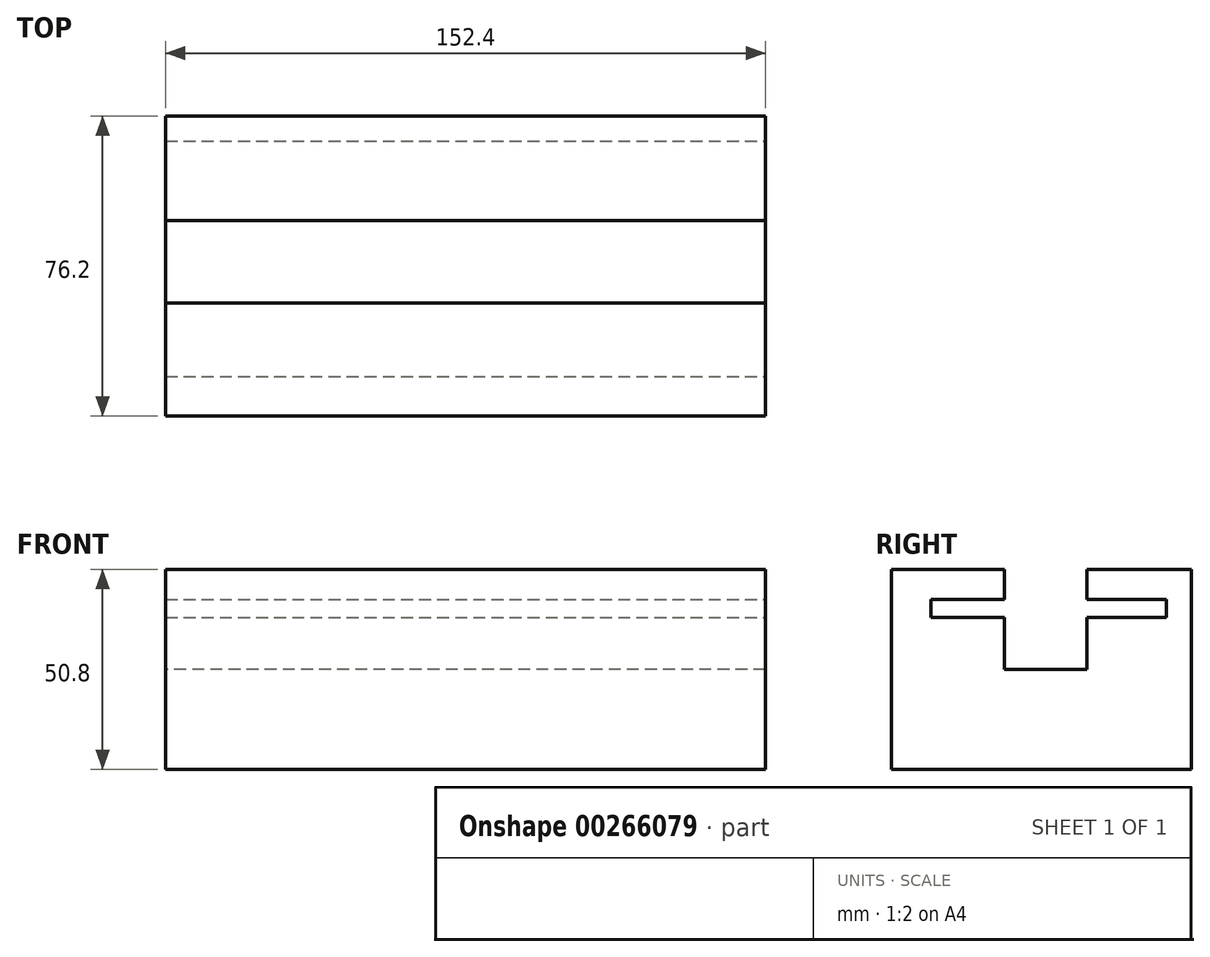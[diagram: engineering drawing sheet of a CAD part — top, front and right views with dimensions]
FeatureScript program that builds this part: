
annotation { "Feature Type Name" : "Feature", "Feature Type Description" : "" }
export const myFeature = defineFeature(function(context is Context, id is Id, definition is map)
    precondition{}
    {
        {
            var Q0;
            Q0=qCreatedBy(makeId("Front.planeOp"),FACE);
            var sketch = newSketch(context, id + "F0", { "sketchPlane" : qUnion([Q0])});
            skLineSegment(sketch, "E0.bottom", {"start": v(-80.74, 62.02) * mm, "end": v(71.66, 62.02) * mm});
            skLineSegment(sketch, "E0.top", {"start": v(-80.74, 11.22) * mm, "end": v(71.66, 11.22) * mm});
            skLineSegment(sketch, "E0.left", {"start": v(-80.74, 62.02) * mm, "end": v(-80.74, 11.22) * mm});
            skLineSegment(sketch, "E0.right", {"start": v(71.66, 62.02) * mm, "end": v(71.66, 11.22) * mm});
            skSolve(sketch);
        }
        {
            var Q0;
            Q0=makeQuery(id+"F0.imprint","IMPRINT",FACE,{"disambiguationData":[TD([[makeQuery(id+"F0.imprint","IMPRINT",EDGE,{"derivedFrom":sQuery(id+"F0.wireOp",EDGE,"E0.bottom")}),-1.0]])]});
            extrude(context, id + "F1", {"entities" : qUnion([Q0]), "depth" : 76.2 * mm});
        }
        {
            var Q0;
            Q0=makeQuery(id+"F1.opExtrude","SWEPT_FACE",FACE,{"disambiguationData":[OSD([sQuery(id+"F0.wireOp",EDGE,"E0.right")])]});
            var sketch = newSketch(context, id + "F2", { "sketchPlane" : qUnion([Q0])});
            skLineSegment(sketch, "E1.bottom", {"start": v(-66.2, 54.4) * mm, "end": v(-6.33, 54.4) * mm});
            skLineSegment(sketch, "E1.top", {"start": v(-66.2, 49.8) * mm, "end": v(-6.33, 49.8) * mm});
            skLineSegment(sketch, "E1.left", {"start": v(-66.2, 54.4) * mm, "end": v(-66.2, 49.8) * mm});
            skLineSegment(sketch, "E1.right", {"start": v(-6.33, 54.4) * mm, "end": v(-6.33, 49.8) * mm});
            skSolve(sketch);
        }
        {
            var Q0;
            Q0=makeQuery(id+"F2.imprint","IMPRINT",FACE,{"disambiguationData":[TD([[makeQuery(id+"F2.imprint","IMPRINT",EDGE,{"derivedFrom":sQuery(id+"F2.wireOp",EDGE,"E1.bottom")}),-1.0]])]});
            extrude(context, id + "F3", {"entities" : qUnion([Q0]), "operationType" : NewBodyOperationType.REMOVE, "endBound" : BoundingType.UP_TO_NEXT, "oppositeDirection" : true, "depth" : 25.4 * mm});
        }
        {
            var Q0;
            Q0=makeQuery(id+"F1.opExtrude","SWEPT_FACE",FACE,{"disambiguationData":[OSD([sQuery(id+"F0.wireOp",EDGE,"E0.bottom")])]});
            var sketch = newSketch(context, id + "F4", { "sketchPlane" : qUnion([Q0])});
            skLineSegment(sketch, "E2.bottom", {"start": v(71.66, -26.55) * mm, "end": v(-80.74, -26.55) * mm});
            skLineSegment(sketch, "E2.top", {"start": v(71.66, -47.44) * mm, "end": v(-80.74, -47.44) * mm});
            skLineSegment(sketch, "E2.left", {"start": v(71.66, -26.55) * mm, "end": v(71.66, -47.44) * mm});
            skLineSegment(sketch, "E2.right", {"start": v(-80.74, -26.55) * mm, "end": v(-80.74, -47.44) * mm});
            skSolve(sketch);
        }
        {
            var Q0;
            Q0=makeQuery(id+"F4.imprint","IMPRINT",FACE,{"disambiguationData":[TD([[makeQuery(id+"F4.imprint","IMPRINT",EDGE,{"derivedFrom":sQuery(id+"F4.wireOp",EDGE,"E2.bottom")}),1.0]])]});
            extrude(context, id + "F5", {"entities" : qUnion([Q0]), "operationType" : NewBodyOperationType.REMOVE, "oppositeDirection" : true, "depth" : 25.4 * mm});
        }
    });
